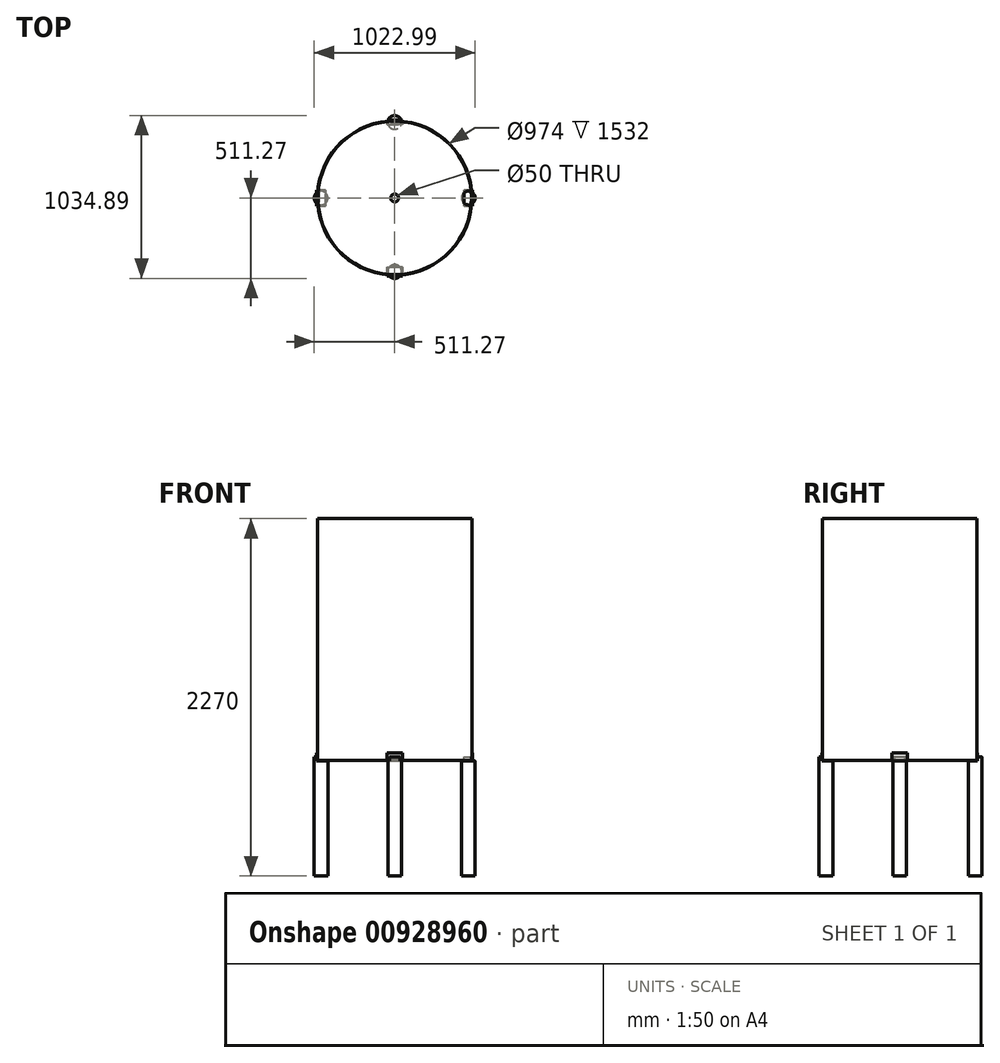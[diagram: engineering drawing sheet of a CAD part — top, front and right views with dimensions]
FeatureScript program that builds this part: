
annotation { "Feature Type Name" : "Feature", "Feature Type Description" : "" }
export const myFeature = defineFeature(function(context is Context, id is Id, definition is map)
    precondition{}
    {
        {
            var Q0;
            Q0=qCreatedBy(makeId("Top.planeOp"),FACE);
            var sketch = newSketch(context, id + "F0", { "sketchPlane" : qUnion([Q0])});
            skCircle(sketch, "E0", {"center": v(0, 0) * mm, "radius": 490 * mm});
            skSolve(sketch);
        }
        {
            var Q0;
            Q0 = qSketchRegion(id + "F0", true);
            extrude(context, id + "F1", {"entities" : qUnion([Q0]), "depth" : 1535 * mm, "offsetDistance" : 25.4 * mm});
        }
        {
            var Q0;
            Q0=makeQuery(id+"F1.opExtrude","CAP_FACE",FACE,{"disambiguationData":[OSD([sQuery(id+"F0.wireOp",EDGE,"E0")])],"isStart":false});
            shell(context, id + "F2", {"entities" : qUnion([Q0]), "thickness" : 3 * mm});
        }
        {
            var Q0;
            Q0=makeQuery(id+"F1.opExtrude","CAP_EDGE",EDGE,{"disambiguationData":[OSD([sQuery(id+"F0.wireOp",EDGE,"E0")])],"isStart":true});
            fillet(context, id + "F3", {"entities" : qUnion([Q0]), "radius" : 10 * mm, "tangentPropagation" : true, "allowEdgeOverflow" : false});
        }
        {
            var Q0;
            Q0=qCreatedBy(makeId("Front.planeOp"),FACE);
            cPlane(context, id + "F4", {"entities" : qUnion([Q0]), "cplaneType" : CPlaneType.OFFSET, "offset" : 490.02 * mm, "width" : 152.4 * mm, "height" : 152.4 * mm});
        }
        {
            var Q0;
            Q0=qCreatedBy(id+"F4.planeOp",FACE);
            var sketch = newSketch(context, id + "F5", { "sketchPlane" : qUnion([Q0])});
            skLineSegment(sketch, "E1.bottom", {"start": v(-50, 45) * mm, "end": v(50, 45) * mm});
            skLineSegment(sketch, "E1.top", {"start": v(-50, -5) * mm, "end": v(50, -5) * mm});
            skLineSegment(sketch, "E1.left", {"start": v(-50, 45) * mm, "end": v(-50, -5) * mm});
            skLineSegment(sketch, "E1.right", {"start": v(50, 45) * mm, "end": v(50, -5) * mm});
            skLineSegment(sketch, "E2", {"start": v(0, 204.8) * mm, "end": v(0, -95.52) * mm, "construction": true});
            skSolve(sketch);
        }
        {
            var Q0;
            Q0 = qSketchRegion(id + "F5", true);
            extrude(context, id + "F6", {"entities" : qUnion([Q0]), "depth" : 5 * mm, "offsetDistance" : 25.4 * mm});
        }
        {
            var Q0;
            Q0=makeQuery(id+"F6.opExtrude","CAP_FACE",FACE,{"disambiguationData":[OSD([sQuery(id+"F5.wireOp",EDGE,"E1.bottom"),sQuery(id+"F5.wireOp",EDGE,"E1.top"),sQuery(id+"F5.wireOp",EDGE,"E1.left"),sQuery(id+"F5.wireOp",EDGE,"E1.right")])],"isStart":true});
            var sketch = newSketch(context, id + "F7", { "sketchPlane" : qUnion([Q0])});
            skLineSegment(sketch, "E3.bottom", {"start": v(-50, -5) * mm, "end": v(50, -5) * mm});
            skLineSegment(sketch, "E3.top", {"start": v(-50, 0) * mm, "end": v(50, 0) * mm});
            skLineSegment(sketch, "E3.left", {"start": v(-50, -5) * mm, "end": v(-50, 0) * mm});
            skLineSegment(sketch, "E3.right", {"start": v(50, -5) * mm, "end": v(50, 0) * mm});
            skSolve(sketch);
        }
        {
            var Q0;
            Q0 = qSketchRegion(id + "F7", true);
            extrude(context, id + "F8", {"entities" : qUnion([Q0]), "operationType" : NewBodyOperationType.ADD, "depth" : 50 * mm, "offsetDistance" : 25.4 * mm});
        }
        {
            var Q0;
            Q0=qCreatedBy(makeId("Right.planeOp"),FACE);
            cPlane(context, id + "F9", {"entities" : qUnion([Q0]), "cplaneType" : CPlaneType.OFFSET, "offset" : 490.47 * mm, "width" : 152.4 * mm, "height" : 152.4 * mm});
        }
        {
            var Q0;
            Q0=qCreatedBy(id+"F9.planeOp",FACE);
            var sketch = newSketch(context, id + "F10", { "sketchPlane" : qUnion([Q0])});
            skLineSegment(sketch, "E4.bottom", {"start": v(-50, 45) * mm, "end": v(50, 45) * mm});
            skLineSegment(sketch, "E4.top", {"start": v(-50, -5) * mm, "end": v(50, -5) * mm});
            skLineSegment(sketch, "E4.left", {"start": v(-50, 45) * mm, "end": v(-50, -5) * mm});
            skLineSegment(sketch, "E4.right", {"start": v(50, 45) * mm, "end": v(50, -5) * mm});
            skLineSegment(sketch, "E5", {"start": v(0, 61.17) * mm, "end": v(0, -57.43) * mm, "construction": true});
            skSolve(sketch);
        }
        {
            var Q0;
            Q0 = qSketchRegion(id + "F10", true);
            extrude(context, id + "F11", {"entities" : qUnion([Q0]), "depth" : 5 * mm, "offsetDistance" : 25.4 * mm});
        }
        {
            var Q0;
            Q0=makeQuery(id+"F11.opExtrude","CAP_FACE",FACE,{"disambiguationData":[OSD([sQuery(id+"F10.wireOp",EDGE,"E4.bottom"),sQuery(id+"F10.wireOp",EDGE,"E4.top"),sQuery(id+"F10.wireOp",EDGE,"E4.left"),sQuery(id+"F10.wireOp",EDGE,"E4.right")])],"isStart":true});
            var sketch = newSketch(context, id + "F12", { "sketchPlane" : qUnion([Q0])});
            skLineSegment(sketch, "E6.bottom", {"start": v(-50, -5) * mm, "end": v(50, -5) * mm});
            skLineSegment(sketch, "E6.top", {"start": v(-50, 0) * mm, "end": v(50, 0) * mm});
            skLineSegment(sketch, "E6.left", {"start": v(-50, -5) * mm, "end": v(-50, 0) * mm});
            skLineSegment(sketch, "E6.right", {"start": v(50, -5) * mm, "end": v(50, 0) * mm});
            skSolve(sketch);
        }
        {
            var Q0;
            Q0 = qSketchRegion(id + "F12", true);
            extrude(context, id + "F13", {"entities" : qUnion([Q0]), "operationType" : NewBodyOperationType.ADD, "depth" : 50 * mm, "offsetDistance" : 25.4 * mm});
        }
        {
            var Q0;
            Q0=qCreatedBy(makeId("Right.planeOp"),FACE);
            cPlane(context, id + "F14", {"entities" : qUnion([Q0]), "cplaneType" : CPlaneType.OFFSET, "offset" : 490.02 * mm, "oppositeDirection" : true, "width" : 152.4 * mm, "height" : 152.4 * mm});
        }
        {
            var Q0;
            Q0=qCreatedBy(id+"F14.planeOp",FACE);
            var sketch = newSketch(context, id + "F15", { "sketchPlane" : qUnion([Q0])});
            skLineSegment(sketch, "E7", {"start": v(0, 25.43) * mm, "end": v(0, -23.96) * mm, "construction": true});
            skLineSegment(sketch, "E8.bottom", {"start": v(50, 45) * mm, "end": v(-50, 45) * mm});
            skLineSegment(sketch, "E8.top", {"start": v(50, -5) * mm, "end": v(-50, -5) * mm});
            skLineSegment(sketch, "E8.left", {"start": v(50, 45) * mm, "end": v(50, -5) * mm});
            skLineSegment(sketch, "E8.right", {"start": v(-50, 45) * mm, "end": v(-50, -5) * mm});
            skSolve(sketch);
        }
        {
            var Q0;
            Q0 = qSketchRegion(id + "F15", true);
            extrude(context, id + "F16", {"entities" : qUnion([Q0]), "operationType" : NewBodyOperationType.ADD, "oppositeDirection" : true, "depth" : 5 * mm, "offsetDistance" : 25.4 * mm});
        }
        {
            var Q0;
            Q0=makeQuery(id+"F16.opExtrude","CAP_FACE",FACE,{"disambiguationData":[OSD([sQuery(id+"F15.wireOp",EDGE,"E8.bottom"),sQuery(id+"F15.wireOp",EDGE,"E8.top"),sQuery(id+"F15.wireOp",EDGE,"E8.left"),sQuery(id+"F15.wireOp",EDGE,"E8.right")])],"isStart":true});
            var sketch = newSketch(context, id + "F17", { "sketchPlane" : qUnion([Q0])});
            skLineSegment(sketch, "E9.bottom", {"start": v(-50, -5) * mm, "end": v(50, -5) * mm});
            skLineSegment(sketch, "E9.top", {"start": v(-50, 0) * mm, "end": v(50, 0) * mm});
            skLineSegment(sketch, "E9.left", {"start": v(-50, -5) * mm, "end": v(-50, 0) * mm});
            skLineSegment(sketch, "E9.right", {"start": v(50, -5) * mm, "end": v(50, 0) * mm});
            skSolve(sketch);
        }
        {
            var Q0;
            Q0 = qSketchRegion(id + "F17", true);
            extrude(context, id + "F18", {"entities" : qUnion([Q0]), "operationType" : NewBodyOperationType.ADD, "depth" : 50 * mm, "offsetDistance" : 25.4 * mm});
        }
        {
            var Q0;
            Q0=qCreatedBy(makeId("Front.planeOp"),FACE);
            cPlane(context, id + "F19", {"entities" : qUnion([Q0]), "cplaneType" : CPlaneType.OFFSET, "offset" : 490.07 * mm, "oppositeDirection" : true, "width" : 152.4 * mm, "height" : 152.4 * mm});
        }
        {
            var Q0;
            Q0=qCreatedBy(id+"F19.planeOp",FACE);
            var sketch = newSketch(context, id + "F20", { "sketchPlane" : qUnion([Q0])});
            skLineSegment(sketch, "E10.bottom", {"start": v(50, 45) * mm, "end": v(-50, 45) * mm});
            skLineSegment(sketch, "E10.top", {"start": v(50, -5) * mm, "end": v(-50, -5) * mm});
            skLineSegment(sketch, "E10.left", {"start": v(50, 45) * mm, "end": v(50, -5) * mm});
            skLineSegment(sketch, "E10.right", {"start": v(-50, 45) * mm, "end": v(-50, -5) * mm});
            skLineSegment(sketch, "E11", {"start": v(0, 62.6) * mm, "end": v(0, -36.94) * mm, "construction": true});
            skSolve(sketch);
        }
        {
            var Q0;
            Q0 = qSketchRegion(id + "F20", true);
            extrude(context, id + "F21", {"entities" : qUnion([Q0]), "operationType" : NewBodyOperationType.ADD, "oppositeDirection" : true, "depth" : 5 * mm, "offsetDistance" : 25.4 * mm});
        }
        {
            var Q0;
            Q0=makeQuery(id+"F21.opExtrude","CAP_FACE",FACE,{"disambiguationData":[OSD([sQuery(id+"F20.wireOp",EDGE,"E10.bottom"),sQuery(id+"F20.wireOp",EDGE,"E10.top"),sQuery(id+"F20.wireOp",EDGE,"E10.left"),sQuery(id+"F20.wireOp",EDGE,"E10.right")])],"isStart":true});
            var sketch = newSketch(context, id + "F22", { "sketchPlane" : qUnion([Q0])});
            skLineSegment(sketch, "E12.bottom", {"start": v(-50, -5) * mm, "end": v(50, -5) * mm});
            skLineSegment(sketch, "E12.top", {"start": v(-50, 0) * mm, "end": v(50, 0) * mm});
            skLineSegment(sketch, "E12.left", {"start": v(-50, -5) * mm, "end": v(-50, 0) * mm});
            skLineSegment(sketch, "E12.right", {"start": v(50, -5) * mm, "end": v(50, 0) * mm});
            skSolve(sketch);
        }
        {
            var Q0;
            Q0 = qSketchRegion(id + "F22", true);
            extrude(context, id + "F23", {"entities" : qUnion([Q0]), "operationType" : NewBodyOperationType.ADD, "depth" : 25.4 * mm, "offsetDistance" : 25.4 * mm});
        }
        {
            var Q0;
            Q0=makeQuery(id+"F13.boolean.opBoolean","MERGE",FACE,{"derivedFrom":[makeQuery(id+"F11.opExtrude","SWEPT_FACE",FACE,{"disambiguationData":[OSD([sQuery(id+"F10.wireOp",EDGE,"E4.top")])]}),makeQuery(id+"F13.opExtrude","SWEPT_FACE",FACE,{"disambiguationData":[OSD([sQuery(id+"F12.wireOp",EDGE,"E6.bottom")])]})]});
            var sketch = newSketch(context, id + "F24", { "sketchPlane" : qUnion([Q0])});
            skCircle(sketch, "E13", {"center": v(467.97, 0) * mm, "radius": 43.75 * mm});
            skLineSegment(sketch, "E14", {"start": v(467.97, 88.93) * mm, "end": v(467.97, 62.28) * mm, "construction": true});
            skPoint(sketch, "E14.startSnap0", {"position": v(467.97, 50) * mm});
            skSolve(sketch);
        }
        {
            var Q0;
            {var subQ0=sQuery(id+"F24.wireOp",EDGE,"E13");var subQ1=makeQuery(id+"F11.opExtrude","CAP_EDGE",EDGE,{"disambiguationData":[OSD([sQuery(id+"F10.wireOp",EDGE,"E4.top")])],"isStart":false});var subQ2=makeQuery(id+"F24.imprint","INTERSECT",VERTEX,{"disambiguationData":[OD(0.0)],"derivedFrom":[subQ1,subQ0]});Q0=makeQuery(id+"F24.imprint","IMPRINT",FACE,{"disambiguationData":[TD([[makeQuery(id+"F24.imprint","IMPRINT",EDGE,{"disambiguationData":[TD([[subQ2,1.0]])],"derivedFrom":subQ0}),1.0]])]});}
            extrude(context, id + "F25", {"entities" : qUnion([Q0]), "operationType" : NewBodyOperationType.ADD, "depth" : 730 * mm, "offsetDistance" : 25.4 * mm, "hasSecondDirection" : true, "secondDirectionOppositeDirection" : true, "secondDirectionDepth" : 25.4 * mm});
        }
        {
            var Q0;
            Q0 = qSketchRegion(id + "F24", true);
            extrude(context, id + "F26", {"entities" : qUnion([Q0]), "operationType" : NewBodyOperationType.ADD, "depth" : 730 * mm, "offsetDistance" : 25.4 * mm});
        }
        {
            var Q0;
            Q0=makeQuery(id+"F8.boolean.opBoolean","MERGE",FACE,{"derivedFrom":[makeQuery(id+"F6.opExtrude","SWEPT_FACE",FACE,{"disambiguationData":[OSD([sQuery(id+"F5.wireOp",EDGE,"E1.top")])]}),makeQuery(id+"F8.opExtrude","SWEPT_FACE",FACE,{"disambiguationData":[OSD([sQuery(id+"F7.wireOp",EDGE,"E3.bottom")])]})]});
            var sketch = newSketch(context, id + "F27", { "sketchPlane" : qUnion([Q0])});
            skLineSegment(sketch, "E15", {"start": v(-86.07, 467.52) * mm, "end": v(72.86, 467.52) * mm, "construction": true});
            skPoint(sketch, "E15.startSnap0", {"position": v(-50, 467.52) * mm});
            skCircle(sketch, "E16", {"center": v(0, 467.52) * mm, "radius": 43.75 * mm});
            skSolve(sketch);
        }
        {
            var Q0;
            Q0 = qSketchRegion(id + "F27", true);
            extrude(context, id + "F28", {"entities" : qUnion([Q0]), "operationType" : NewBodyOperationType.ADD, "depth" : 730 * mm, "offsetDistance" : 25.4 * mm});
        }
        {
            var Q0;
            {var subQ0=sQuery(id+"F5.wireOp",EDGE,"E1.top");var subQ1=sQuery(id+"F27.wireOp",EDGE,"E16");Q0=makeQuery(id+"F28.boolean.opBoolean","SPLIT",FACE,{"disambiguationData":[TD([makeQuery(id+"F6.opExtrude","CAP_FACE",FACE,{"disambiguationData":[OSD([sQuery(id+"F5.wireOp",EDGE,"E1.bottom"),subQ0,sQuery(id+"F5.wireOp",EDGE,"E1.left"),sQuery(id+"F5.wireOp",EDGE,"E1.right")])],"isStart":false})])],"derivedFrom":makeQuery(id+"F28.opExtrude","CAP_FACE",FACE,{"disambiguationData":[OSD([subQ1])],"isStart":true})});}
            var sketch = newSketch(context, id + "F29", { "sketchPlane" : qUnion([Q0])});
            skLineSegment(sketch, "E17", {"start": v(-34.03, -495.02) * mm, "end": v(34.03, -495.02) * mm});
            skArc(sketch, "E18", {"start": v(-34.03, -495.02) * mm, "mid": v(0, -511.27) * mm, "end": v(34.03, -495.02) * mm});
            skSolve(sketch);
        }
        {
            var Q0;
            Q0 = qSketchRegion(id + "F29", true);
            extrude(context, id + "F30", {"entities" : qUnion([Q0]), "operationType" : NewBodyOperationType.ADD, "depth" : 25.4 * mm, "offsetDistance" : 25.4 * mm});
        }
        {
            var Q0;
            Q0=makeQuery(id+"F18.boolean.opBoolean","MERGE",FACE,{"derivedFrom":[makeQuery(id+"F16.opExtrude","SWEPT_FACE",FACE,{"disambiguationData":[OSD([sQuery(id+"F15.wireOp",EDGE,"E8.top")])]}),makeQuery(id+"F18.opExtrude","SWEPT_FACE",FACE,{"disambiguationData":[OSD([sQuery(id+"F17.wireOp",EDGE,"E9.bottom")])]})]});
            var sketch = newSketch(context, id + "F31", { "sketchPlane" : qUnion([Q0])});
            skLineSegment(sketch, "E19", {"start": v(-467.52, -74.57) * mm, "end": v(-467.52, 74.62) * mm, "construction": true});
            skPoint(sketch, "E19.startSnap0", {"position": v(-467.52, -50) * mm});
            skCircle(sketch, "E20", {"center": v(-467.52, 0) * mm, "radius": 43.75 * mm});
            skSolve(sketch);
        }
        {
            var Q0;
            Q0 = qSketchRegion(id + "F31", true);
            extrude(context, id + "F32", {"entities" : qUnion([Q0]), "operationType" : NewBodyOperationType.ADD, "depth" : 730 * mm, "offsetDistance" : 25.4 * mm});
        }
        {
            var Q0;
            {var subQ0=sQuery(id+"F15.wireOp",EDGE,"E8.top");var subQ1=sQuery(id+"F31.wireOp",EDGE,"E20");Q0=makeQuery(id+"F32.boolean.opBoolean","SPLIT",FACE,{"disambiguationData":[TD([makeQuery(id+"F16.opExtrude","CAP_FACE",FACE,{"disambiguationData":[OSD([sQuery(id+"F15.wireOp",EDGE,"E8.bottom"),subQ0,sQuery(id+"F15.wireOp",EDGE,"E8.left"),sQuery(id+"F15.wireOp",EDGE,"E8.right")])],"isStart":false})])],"derivedFrom":makeQuery(id+"F32.opExtrude","CAP_FACE",FACE,{"disambiguationData":[OSD([subQ1])],"isStart":true})});}
            var sketch = newSketch(context, id + "F33", { "sketchPlane" : qUnion([Q0])});
            skLineSegment(sketch, "E21", {"start": v(-495.02, 34.03) * mm, "end": v(-495.02, -34.03) * mm});
            skArc(sketch, "E22", {"start": v(-495.02, 34.03) * mm, "mid": v(-511.27, 0) * mm, "end": v(-495.02, -34.03) * mm});
            skSolve(sketch);
        }
        {
            var Q0;
            Q0 = qSketchRegion(id + "F33", true);
            extrude(context, id + "F34", {"entities" : qUnion([Q0]), "operationType" : NewBodyOperationType.ADD, "depth" : 25.4 * mm, "offsetDistance" : 25.4 * mm});
        }
        {
            var Q0;
            Q0=makeQuery(id+"F23.boolean.opBoolean","MERGE",FACE,{"derivedFrom":[makeQuery(id+"F21.opExtrude","SWEPT_FACE",FACE,{"disambiguationData":[OSD([sQuery(id+"F20.wireOp",EDGE,"E10.top")])]}),makeQuery(id+"F23.opExtrude","SWEPT_FACE",FACE,{"disambiguationData":[OSD([sQuery(id+"F22.wireOp",EDGE,"E12.bottom")])]})]});
            var sketch = newSketch(context, id + "F35", { "sketchPlane" : qUnion([Q0])});
            skLineSegment(sketch, "E23", {"start": v(65.66, -479.87) * mm, "end": v(-74.17, -479.87) * mm, "construction": true});
            skPoint(sketch, "E23.startSnap0", {"position": v(50, -479.87) * mm});
            skCircle(sketch, "E24", {"center": v(0, -479.87) * mm, "radius": 43.75 * mm});
            skSolve(sketch);
        }
        {
            var Q0;
            Q0 = qSketchRegion(id + "F35", true);
            extrude(context, id + "F36", {"entities" : qUnion([Q0]), "operationType" : NewBodyOperationType.ADD, "depth" : 730 * mm, "offsetDistance" : 25.4 * mm});
        }
        {
            var Q0;
            {var subQ0=sQuery(id+"F20.wireOp",EDGE,"E10.top");var subQ1=sQuery(id+"F35.wireOp",EDGE,"E24");Q0=makeQuery(id+"F36.boolean.opBoolean","SPLIT",FACE,{"disambiguationData":[TD([makeQuery(id+"F21.opExtrude","CAP_FACE",FACE,{"disambiguationData":[OSD([sQuery(id+"F20.wireOp",EDGE,"E10.bottom"),subQ0,sQuery(id+"F20.wireOp",EDGE,"E10.left"),sQuery(id+"F20.wireOp",EDGE,"E10.right")])],"isStart":false})])],"derivedFrom":makeQuery(id+"F36.opExtrude","CAP_FACE",FACE,{"disambiguationData":[OSD([subQ1])],"isStart":true})});}
            var sketch = newSketch(context, id + "F37", { "sketchPlane" : qUnion([Q0])});
            skLineSegment(sketch, "E25", {"start": v(41.02, 495.07) * mm, "end": v(-41.02, 495.07) * mm});
            skArc(sketch, "E26", {"start": v(41.02, 495.07) * mm, "mid": v(0, 523.62) * mm, "end": v(-41.02, 495.07) * mm});
            skSolve(sketch);
        }
        {
            var Q0;
            Q0 = qSketchRegion(id + "F37", true);
            extrude(context, id + "F38", {"entities" : qUnion([Q0]), "operationType" : NewBodyOperationType.ADD, "depth" : 25.4 * mm, "offsetDistance" : 25.4 * mm});
        }
        {
            var Q0;
            {var subQ0=sQuery(id+"F0.wireOp",EDGE,"E0");Q0=makeQuery(id+"F2.opShell","OFFSET_FACE",FACE,{"disambiguationData":[OSD([subQ0]),TDD([makeQuery(id+"F1.opExtrude","CAP_FACE",FACE,{"disambiguationData":[OSD([subQ0])],"isStart":true})])]});}
            var sketch = newSketch(context, id + "F39", { "sketchPlane" : qUnion([Q0])});
            skCircle(sketch, "E27", {"center": v(0, 0) * mm, "radius": 25 * mm});
            skSolve(sketch);
        }
        {
            var Q0;
            Q0 = qSketchRegion(id + "F39", true);
            extrude(context, id + "F40", {"entities" : qUnion([Q0]), "operationType" : NewBodyOperationType.REMOVE, "oppositeDirection" : true, "depth" : 25.4 * mm, "offsetDistance" : 25.4 * mm});
        }
    });
